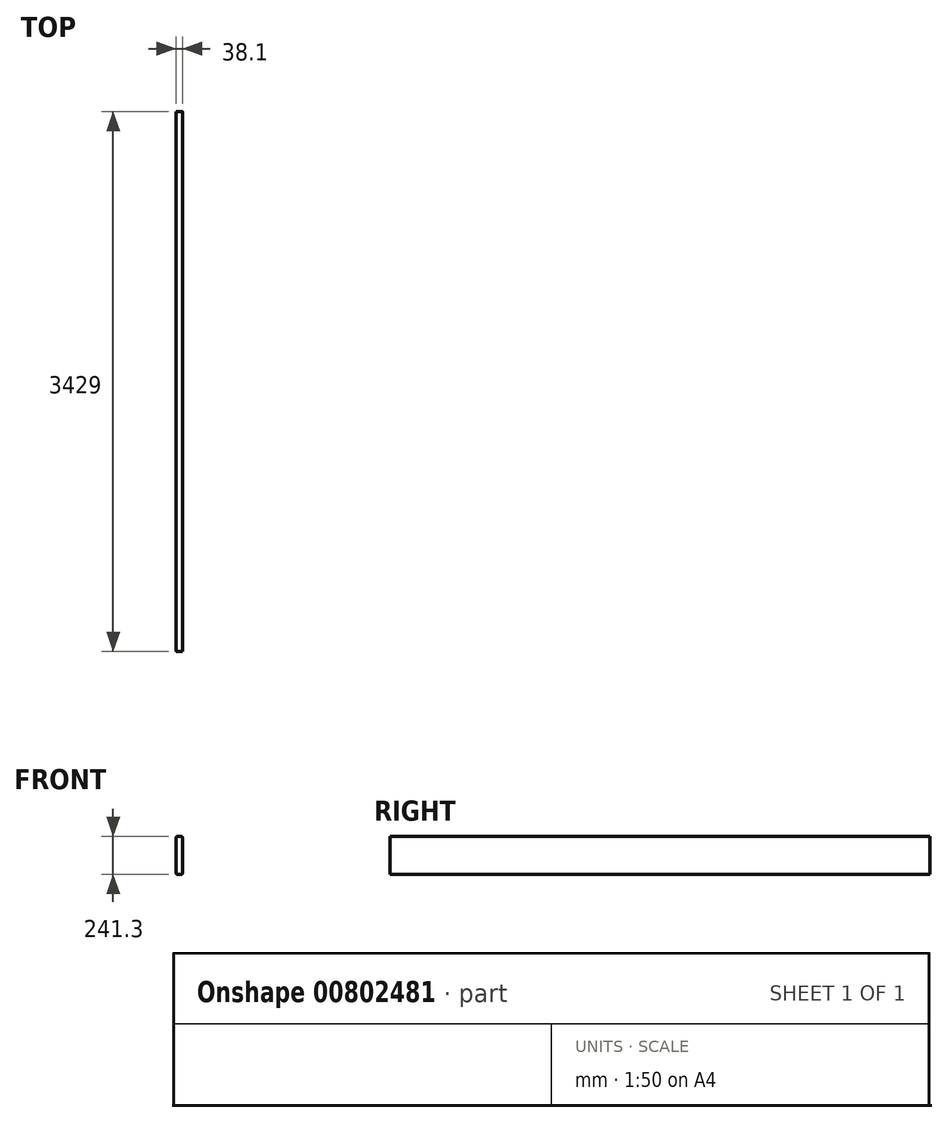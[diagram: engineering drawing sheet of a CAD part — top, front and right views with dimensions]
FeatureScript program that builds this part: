
annotation { "Feature Type Name" : "Feature", "Feature Type Description" : "" }
export const myFeature = defineFeature(function(context is Context, id is Id, definition is map)
    precondition{}
    {
        {
            var Q0;
            Q0=qCreatedBy(makeId("Front.planeOp"),FACE);
            var sketch = newSketch(context, id + "F0", { "sketchPlane" : qUnion([Q0])});
            skLineSegment(sketch, "E0.bottom", {"start": v(-14.22, 120.65) * mm, "end": v(14.22, 120.65) * mm});
            skLineSegment(sketch, "E0.top", {"start": v(-14.22, -120.65) * mm, "end": v(14.22, -120.65) * mm});
            skLineSegment(sketch, "E0.left", {"start": v(-19.05, 115.82) * mm, "end": v(-19.05, -115.82) * mm});
            skLineSegment(sketch, "E0.right", {"start": v(19.05, 115.82) * mm, "end": v(19.05, -115.82) * mm});
            skPoint(sketch, "E0.middle", {"position": v(0, 0) * mm});
            skPoint(sketch, "E1.visualSharp", {"position": v(-19.05, 120.65) * mm});
            skArc(sketch, "E1.filletArc", {"start": v(-14.22, 120.65) * mm, "mid": v(-17.64, 119.24) * mm, "end": v(-19.05, 115.82) * mm});
            skPoint(sketch, "E2.visualSharp", {"position": v(19.05, 120.65) * mm});
            skArc(sketch, "E2.filletArc", {"start": v(19.05, 115.82) * mm, "mid": v(17.64, 119.24) * mm, "end": v(14.22, 120.65) * mm});
            skPoint(sketch, "E3.visualSharp", {"position": v(19.05, -120.65) * mm});
            skArc(sketch, "E3.filletArc", {"start": v(14.22, -120.65) * mm, "mid": v(17.64, -119.24) * mm, "end": v(19.05, -115.82) * mm});
            skPoint(sketch, "E4.visualSharp", {"position": v(-19.05, -120.65) * mm});
            skArc(sketch, "E4.filletArc", {"start": v(-19.05, -115.82) * mm, "mid": v(-17.64, -119.24) * mm, "end": v(-14.22, -120.65) * mm});
            skSolve(sketch);
        }
        {
            var Q0;
            Q0=makeQuery(id+"F0.imprint","IMPRINT",FACE,{"disambiguationData":[TD([[makeQuery(id+"F0.imprint","IMPRINT",EDGE,{"derivedFrom":sQuery(id+"F0.wireOp",EDGE,"E0.bottom")}),-1.0]])]});
            extrude(context, id + "F1", {"entities" : qUnion([Q0]), "endBound" : BoundingType.SYMMETRIC, "depth" : 3429 * mm, "offsetDistance" : 25.4 * mm});
        }
    });
